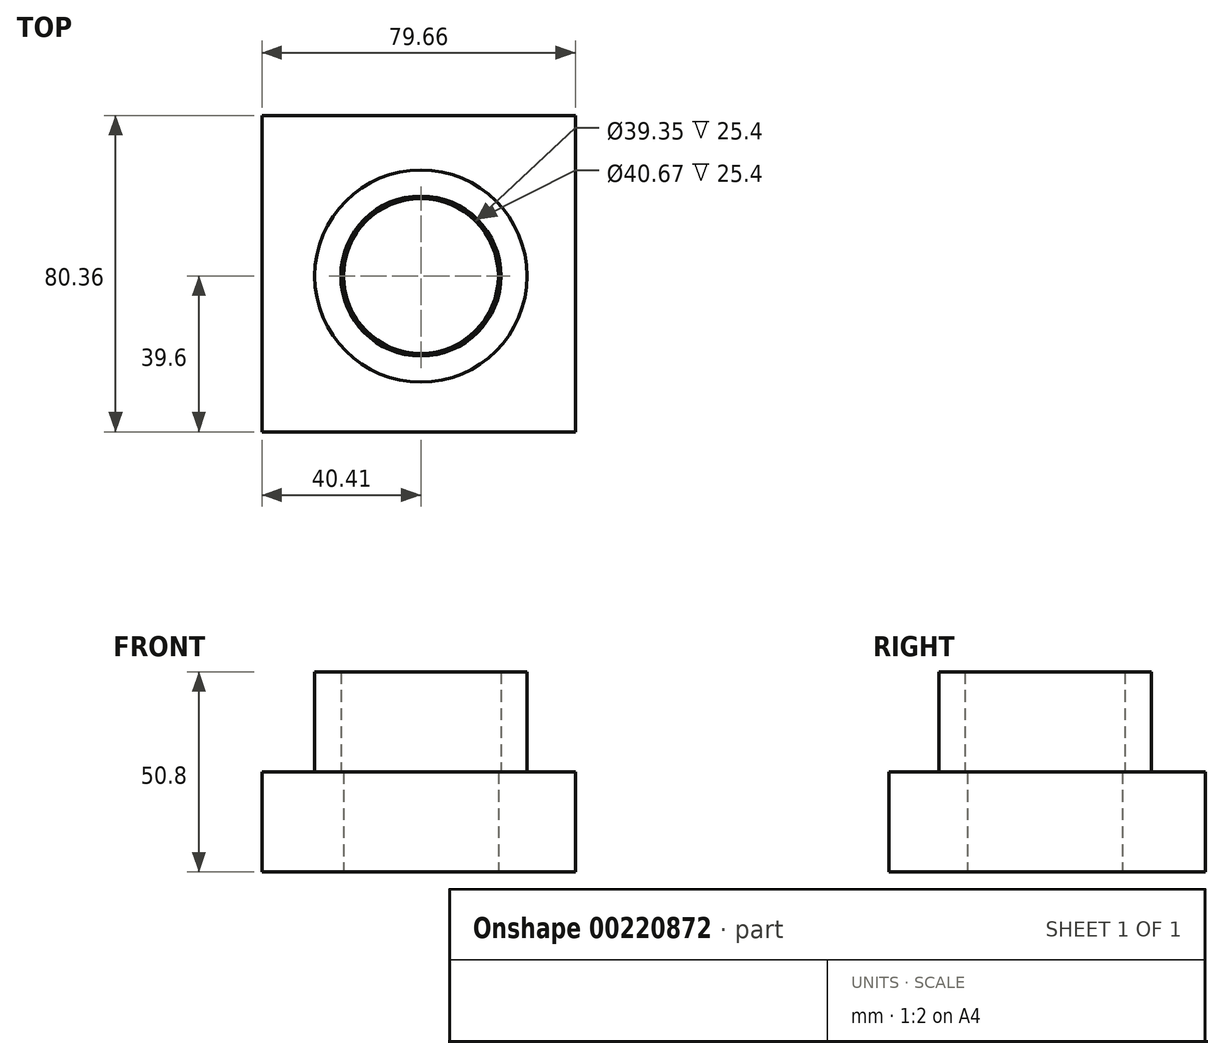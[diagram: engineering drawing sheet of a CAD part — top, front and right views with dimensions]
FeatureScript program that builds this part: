
annotation { "Feature Type Name" : "Feature", "Feature Type Description" : "" }
export const myFeature = defineFeature(function(context is Context, id is Id, definition is map)
    precondition{}
    {
        {
            var Q0;
            Q0=qCreatedBy(makeId("Top.planeOp"),FACE);
            var sketch = newSketch(context, id + "F0", { "sketchPlane" : qUnion([Q0])});
            skLineSegment(sketch, "E0.bottom", {"start": v(-40.4, 40.76) * mm, "end": v(39.25, 40.76) * mm});
            skLineSegment(sketch, "E0.top", {"start": v(-40.4, -39.6) * mm, "end": v(39.25, -39.6) * mm});
            skLineSegment(sketch, "E0.left", {"start": v(-40.4, 40.76) * mm, "end": v(-40.4, -39.6) * mm});
            skLineSegment(sketch, "E0.right", {"start": v(39.25, 40.76) * mm, "end": v(39.25, -39.6) * mm});
            skCircle(sketch, "E1", {"center": v(0, 0) * mm, "radius": 19.68 * mm});
            skCircle(sketch, "E2", {"center": v(0, 0) * mm, "radius": 13.15 * mm});
            skSolve(sketch);
        }
        {
            var Q0;
            Q0=makeQuery(id+"F0.imprint","IMPRINT",FACE,{"disambiguationData":[TD([[makeQuery(id+"F0.imprint","IMPRINT",EDGE,{"derivedFrom":sQuery(id+"F0.wireOp",EDGE,"E0.bottom")}),-1.0]])]});
            extrude(context, id + "F1", {"entities" : qUnion([Q0]), "depth" : 25.4 * mm});
        }
        {
            var Q0;
            Q0=makeQuery(id+"F1.opExtrude","CAP_FACE",FACE,{"disambiguationData":[OSD([sQuery(id+"F0.wireOp",EDGE,"E0.bottom"),sQuery(id+"F0.wireOp",EDGE,"E0.top"),sQuery(id+"F0.wireOp",EDGE,"E0.left"),sQuery(id+"F0.wireOp",EDGE,"E0.right"),sQuery(id+"F0.wireOp",EDGE,"E1")])],"isStart":false});
            var sketch = newSketch(context, id + "F2", { "sketchPlane" : qUnion([Q0])});
            skCircle(sketch, "E3", {"center": v(0, 0) * mm, "radius": 20.34 * mm});
            skCircle(sketch, "E4", {"center": v(0, 0) * mm, "radius": 26.96 * mm});
            skSolve(sketch);
        }
        {
            var Q0;
            Q0=makeQuery(id+"F2.imprint","IMPRINT",FACE,{"disambiguationData":[TD([[makeQuery(id+"F2.imprint","IMPRINT",EDGE,{"derivedFrom":sQuery(id+"F2.wireOp",EDGE,"E3")}),-1.0]])]});
            extrude(context, id + "F3", {"entities" : qUnion([Q0]), "operationType" : NewBodyOperationType.ADD, "depth" : 25.4 * mm});
        }
    });
